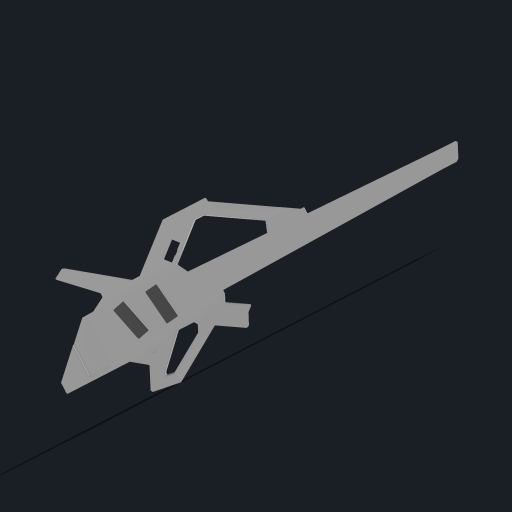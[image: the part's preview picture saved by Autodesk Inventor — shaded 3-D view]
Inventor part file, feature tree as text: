
AUTODESK INVENTOR PART (.ipt)
format: ipt  version: 2023 (Build 270158000, 158)  size: 1,372,672 bytes
history: native  units: in
note: dims shown in document units (in); Inventor stores cm internally (conversion verified against a paired STEP export)
features: other x42, extrude x16, reference x9, fillet x6, sketch x5, projected_geometry x5, chamfer x4, hole x2
ambient origin geometry x8: Origin, YZ Plane, XZ Plane, XY Plane, X Axis, Y Axis, Z Axis, Center Point
bodies: BodySolid (feature_tree), BodyFeature (feature_tree), BodySculptCleanupFeature (feature_tree), BodyFilletsFeature (feature_tree), Body (feature_tree), BodySculptCleanup (feature_tree)
feature tree (89):
  reference  "Reference"
  other  "TopFrontSculptEdge"
  other  "TopFrontSculptFeature"
  other  "TopFrontHandleSculptFeature"
  other  "BottomFrontSculptEdge"
  other  "BottomFrontSculptFeature"
  other  "BottomCleanupFeature"
  other  "BackSculptEdges"
  other  "BackSculptTopFeature"
  other  "BackSculptBottomFeature"
  other  "BackSculptCleanupFeature"
  extrude  "TunersIndentationFeature"  Depth=3.5in
  chamfer  "TunersChamferFeature"  Distance=0.7009in
  other  "Detail"
  extrude  "OscCutFeature"  Depth=0.702in
  fillet  "OscSmallFilletsFeature"  Radius=1.7in
  fillet  "OscLargeFilletsFeature"  Radius=1.017in
  chamfer  "BottomChamfers"  Distance=1.125in
  chamfer  "NeckChamfer"  Distance=7.333in
  extrude  "PickupsFeature"  Depth=0.702in
  fillet  "PickupFilletsFeature"  Radius=0.7009in
  fillet  "GeneralFilletsFeature"  Radius=1.125in
  extrude  "OscCavityCutFeature"  Depth=0.702in
  fillet  "OscCutFilletsFeature"  Radius=0.9826in
  extrude  "OscCoverIndentFeature"  Depth=0.702in
  hole  "OscMountHolesFeature"  [1 undecoded]
  extrude  "KnobsFeature"  Depth=0.702in
  other  "GripsPlane"
  extrude  "GripsPreviewFeature"  Depth=0.702in
  other  "BottomFrontGripIndentPlane"
  other  "BottomBackGripIndentPlane"
  other  "TopFrontGripIndentPlane"
  other  "TopBackGripIndentPlane"
  extrude  "BottomFrontGripIndentFeature"  Depth=0.702in
  extrude  "BottomBackGripIndentFeature"  Depth=0.702in
  chamfer  "BottomFrontGripBevelFeature"  Distance=2.333in
  extrude  "TopFrontGripIndentFeature"  Depth=0.702in
  extrude  "TopBackGripIndentFeature"  Depth=0.702in
  other  "SwitchesPlane"
  sketch  "Sketch33"  dims[d52=120.0deg]
  extrude  "Extrusion23"  Depth=0.702in
  extrude  "Extrusion24"  TaperAngle=120.0deg  [1 undecoded]
  extrude  "Extrusion25"  Depth=0.702in
  extrude  "Extrusion26"  Depth=0.702in
  hole  "Hole2"  [1 undecoded]
  fillet  "Fillet15"  Radius=0.5in
  sketch  "Sketch36"  dims[d54=1.333in]
  extrude  "Extrusion27"  Depth=0.702in
  other  "Front"
  other  "Back"
  other  "Side"
  other  "Pickups"
  other  "TunersIndentation"
  other  "OscCavity"
  other  "OscCoverIndent"
  other  "OscMountHoles"
  other  "TopFrontSculptPlane"
  other  "TopFrontHandleSculptPlane"
  other  "BottomFrontSculptPlane"
  other  "BackSculptTopPlane"
  other  "BackSculptBottomPlane"
  other  "PickupsSolid"
  other  "Knobs"
  other  "Grips"
  other  "GripsSolid"
  sketch  "Sketch27"  dims[d50=0.7833in d51=3.5in]
  other  "BottomBackGripIndent"
  other  "TopFrontGripIndent"
  other  "TopBackGripIndent"
  sketch  "Sketch35"  dims[d53=120.0deg]
  projected_geometry  "Projected Loop2"
  sketch  "Sketch37"  dims[d55=120.0deg d56=0.7009in d58=1.333in d60=1.7in d61=1.017in d62=1.125in d63=7.333in d64=4.75in d65=0.7009in d66=1.125in d67=4.4in d68=0.9826in d70=8.25in d73=2.0in d75=1.5in d78=1.5in d80=12.0in d81=8.25in d83=2.333in d85=3.25in d88=3.75in d89=7.75in d93=120.0deg d94=3.25in d95=0.5in d96=1.5in d97=0.5in d98=5.5in d99=0.5in d100=1.0in d101=3.125in d102=1.0in d104=2.0in d105=0.333in d106=0.5in d108=1.65in d109=0.0in d110=0.25in d111=0.125in d112=45.0deg d113=1.25in d114=1.25in d115=2.0in d117=0.5in d118=0.333in d119=0.0962in d120=1.0in d124=0.25in d125=0.125in d126=45.0deg d127=0.303in d128=0.2792in d129=45.0deg d130=0.4466in d131=0.3161in d132=0.3745in d134=0.0106in d135=0.7902in d136=2.2262in d137=10.4403in d138=2.61in d139=2.7216in d140=0.9208in d141=1.9872in d142=1.6321in d143=5.3192in d145=1.5087in d146=0.7765in d147=0.2542in d148=1.0in d149=0.7in d150=0.9658in d151=0.1718in d152=0.6278in d153=0.6291in d154=0.6305in d155=0.626in d156=0.6209in d157=0.6171in d158=0.6104in d159=0.0458in d160=0.0481in d161=0.0962in d162=0.1718in d163=25.3233in d164=44.5846in d165=44.9997in d166=45.4565in d167=45.8614in d168=46.3233in d169=47.7096in d170=48.4096in d171=50.3233in d172=2.2262in d173=7.2122in d174=10.0378in d175=6.2122in d176=8.0378in d177=1.8694in d178=4.2122in d179=6.7878in d180=1.6in d181=4.5in d182=0.1666in d183=1.1648in d184=35.4267in d185=37.8342in d186=0.8274in d187=41.0927in d188=6.4431in d189=0.7861in d190=1.0531in d191=1.2558in d192=1.493in d193=1.696in d194=2.7725in d195=25.3233in d196=1.7878in d197=5.1041in d198=38.6262in d199=5.4393in d200=44.1389in d201=0.3543in d202=0.0in d203=0.125in d204=0.315in d205=0.0in d206=0.25in d207=0.125in d208=45.0deg d209=2.5in d210=1.031in d211=0.5in d212=0.625in d213=0.063in d214=0.1181in d215=0.0in d216=0.01in d217=0.06in d230=0.125in d231=2.6644in d232=1.4144in d237=0.315in d238=0.0in d239=0.0394in d241=0.0787in d242=0.0in d243=0.0787in d244=0.75in d245=0.4134in d246=0.1181in d247=0.5635in d248=0.1969in d249=0.8108in d250=0.0172in d251=0.0in d252=0.0in d253=-0.0137in d257=0.1917in d258=0.0822in d259=0.0137in d260=0.0137in d261=0.212in d262=0.2095in d263=0.0002in d264=0.6178in d265=0.6188in d266=0.1722in d267=1.548in d278=25.0in d283=0.374in d284=0.75in d285=0.0in d292=1.75in d293=0.0in d310=0.8521in d311=105.0deg d312=0.9in d313=0.1in d314=0.8383in d315=0.8589in d317=0.1358in d318=0.962in d319=0.333in d320=0.7in d321=5.25in d322=0.1819in d323=-0.3937in d324=-0.3937in d325=-0.315in d326=-0.315in d327=1.104in d328=0.0in d329=0.394in d330=0.0in d331=1.104in d332=0.0in d333=0.315in d334=0.0in d335=0.25in d336=0.25in d337=0.25in d338=0.125in d339=45.0deg d341=3.2129in d351=1.0452in d352=0.5in d353=1.0452in d354=0.8101in d355=0.1575in d356=0.9843in d357=0.0in d358=1.0in d359=0.0in d360=0.315in d361=0.0in d362=0.5in d363=0.0in d364=0.0787in d365=0.0787in d366=0.0787in d367=0.0787in d368=0.0787in d369=0.0787in d370=0.0787in d371=0.0787in d372=0.0787in d373=0.0787in d374=0.0787in d375=0.75in d376=0.375in d377=0.25in d378=0.5635in d379=0.315in d380=0.8108in d381=0.125in d382=0.0197in d383=0.0197in d384=0.0197in d385=0.0197in d386=0.702in d387=0.0in d388=1.9173in d389=1.9173in d390=2.7243in]
  reference  "Reference1"
  reference  "Reference2"
  reference  "Reference3"
  reference  "Reference4"
  reference  "Reference5"
  reference  "Reference6"
  reference  "Reference7"
  reference  "Reference8"
  projected_geometry  "Projected Loop4"
  projected_geometry  "Projected Loop5"
  projected_geometry  "Projected Loop6"
  projected_geometry  "Projected Loop7"
  other  "Delete2"
  other  "Delete3"
  other  "<userpath>\Desktop\hybrid\src\Hybrid.iam"
  other  "Hybrid.iam"
  other  "MidiController:1"
note: 3 required parameter values undecoded (feature->parameter linkage not recoverable at this tier; creation-order binding heuristic only, values carry confidence <= 0.55)
